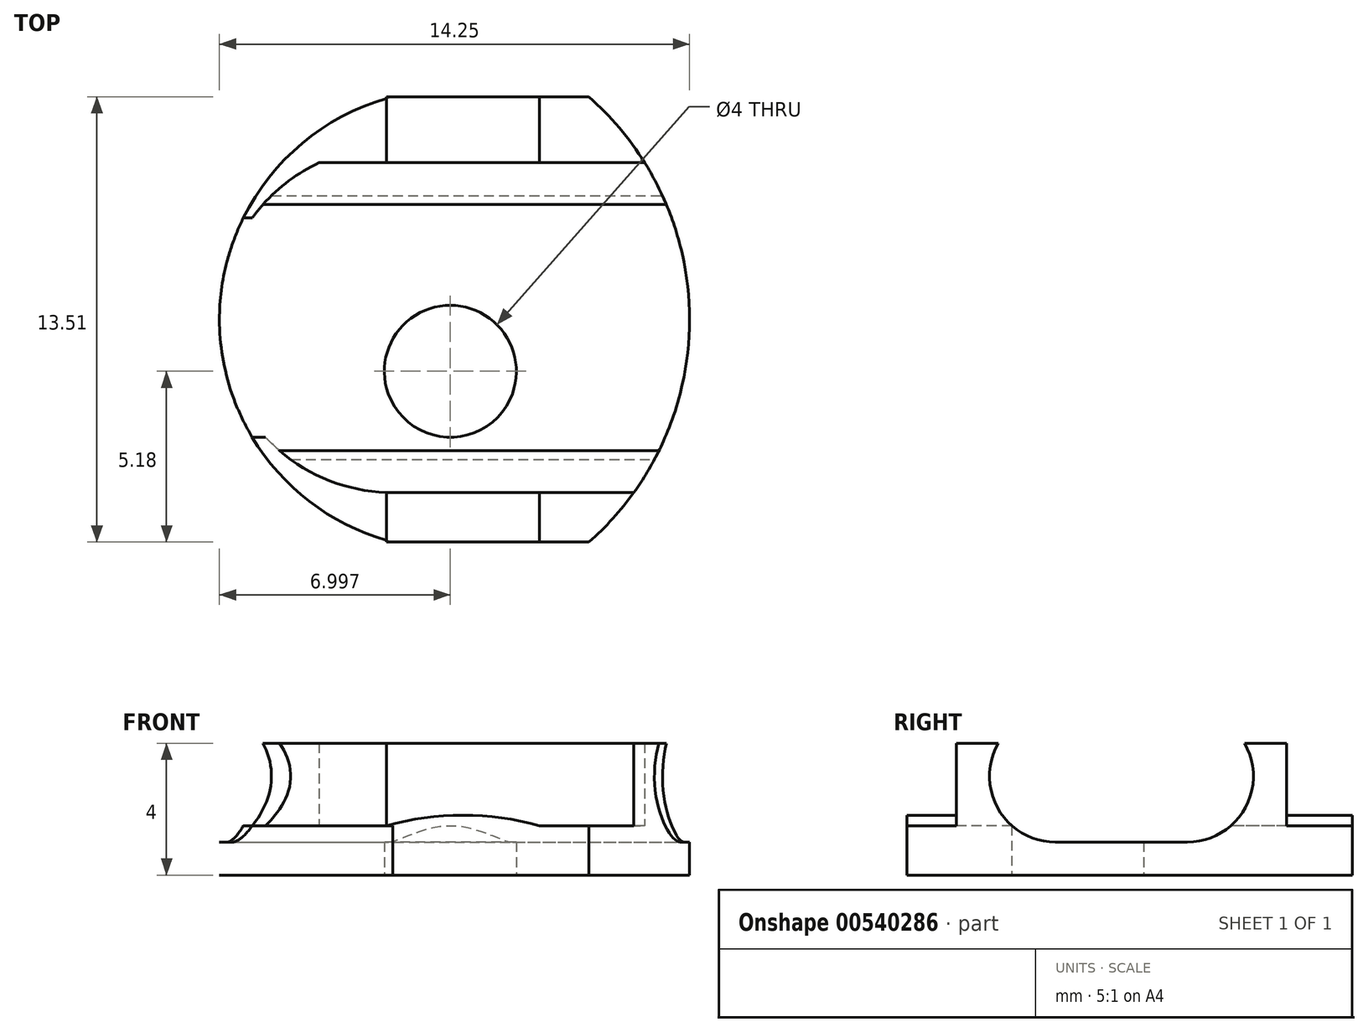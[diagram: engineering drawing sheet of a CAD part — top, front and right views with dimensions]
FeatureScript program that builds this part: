
annotation { "Feature Type Name" : "Feature", "Feature Type Description" : "" }
export const myFeature = defineFeature(function(context is Context, id is Id, definition is map)
    precondition{}
    {
        {
            var Q0;
            Q0=qCreatedBy(makeId("Top.planeOp"),FACE);
            var sketch = newSketch(context, id + "F0", { "sketchPlane" : qUnion([Q0])});
            skArc(sketch, "E0", {"start": v(-37.22, 31.39) * mm, "mid": v(-40.14, 25.58) * mm, "end": v(-35.18, 21.39) * mm});
            skLineSegment(sketch, "E1", {"start": v(-37.22, 31.39) * mm, "end": v(-29.22, 31.39) * mm});
            skLineSegment(sketch, "E2", {"start": v(-35.18, 21.39) * mm, "end": v(-27.87, 21.39) * mm});
            skLineSegment(sketch, "E3", {"start": v(-35, 33.38) * mm, "end": v(-29.04, 33.38) * mm});
            skLineSegment(sketch, "E4", {"start": v(-35, 19.88) * mm, "end": v(-29.04, 19.88) * mm});
            skArc(sketch, "E5", {"start": v(-29.04, 33.38) * mm, "mid": v(-26, 26.63) * mm, "end": v(-29.04, 19.88) * mm});
            skArc(sketch, "E6", {"start": v(-35, 33.38) * mm, "mid": v(-38.77, 30.9) * mm, "end": v(-40.24, 26.63) * mm});
            skArc(sketch, "E7", {"start": v(-40.24, 26.63) * mm, "mid": v(-38.77, 22.36) * mm, "end": v(-35, 19.88) * mm});
            skLineSegment(sketch, "E8.bottom", {"start": v(-29.22, 31.39) * mm, "end": v(-25.22, 31.39) * mm});
            skLineSegment(sketch, "E8.top", {"start": v(-29.22, 21.39) * mm, "end": v(-25.22, 21.39) * mm});
            skLineSegment(sketch, "E8.right", {"start": v(-25.22, 31.39) * mm, "end": v(-25.22, 21.39) * mm});
            skLineSegment(sketch, "E9", {"start": v(-33.24, 26.66) * mm, "end": v(-33.24, 25.06) * mm});
            skCircle(sketch, "E10", {"center": v(-33.24, 25.06) * mm, "radius": 2 * mm});
            skSolve(sketch);
        }
        {
            var Q0;
            {var subQ1=sQuery(id+"F0.wireOp",EDGE,"E1");Q0=makeQuery(id+"F0.imprint","IMPRINT",FACE,{"disambiguationData":[TD([[makeQuery(id+"F0.imprint","IMPRINT",EDGE,{"derivedFrom":subQ1}),-1.0]])]});}
            var Q1;
            {var subQ0=sQuery(id+"F0.wireOp",EDGE,"E8.bottom");Q1=makeQuery(id+"F0.imprint","IMPRINT",FACE,{"disambiguationData":[TD([[makeQuery(id+"F0.imprint","IMPRINT",EDGE,{"derivedFrom":subQ0}),-1.0]])]});}
            var Q2;
            Q2=makeQuery(id+"F0.imprint","IMPRINT",FACE,{"disambiguationData":[TD([[makeQuery(id+"F0.imprint","IMPRINT",EDGE,{"derivedFrom":sQuery(id+"F0.wireOp",EDGE,"E10")}),1.0]])]});
            extrude(context, id + "F1", {"entities" : qUnion([Q0, Q1, Q2]), "depth" : 4 * mm, "offsetDistance" : 25 * mm});
        }
        {
            var Q0;
            {var subQ1=sQuery(id+"F0.wireOp",EDGE,"E1");Q0=makeQuery(id+"F0.imprint","IMPRINT",FACE,{"disambiguationData":[TD([[makeQuery(id+"F0.imprint","IMPRINT",EDGE,{"derivedFrom":subQ1}),1.0]])]});}
            var Q1;
            {var subQ2=sQuery(id+"F0.wireOp",EDGE,"E2");Q1=makeQuery(id+"F0.imprint","IMPRINT",FACE,{"disambiguationData":[TD([[makeQuery(id+"F0.imprint","IMPRINT",EDGE,{"derivedFrom":subQ2}),-1.0]])]});}
            extrude(context, id + "F2", {"entities" : qUnion([Q0, Q1]), "operationType" : NewBodyOperationType.ADD, "depth" : 1.5 * mm, "offsetDistance" : 25 * mm});
        }
        {
            var Q0;
            Q0=makeQuery(id+"F1.opExtrude","SWEPT_FACE",FACE,{"disambiguationData":[OSD([sQuery(id+"F0.wireOp",EDGE,"E2")])]});
            var sketch = newSketch(context, id + "F3", { "sketchPlane" : qUnion([Q0])});
            skLineSegment(sketch, "E11", {"start": v(-29.04, 1.5) * mm, "end": v(-30.54, 1.5) * mm});
            skArc(sketch, "E12", {"start": v(-30.54, 1.5) * mm, "mid": v(-32.86, 1.82) * mm, "end": v(-35.18, 1.5) * mm});
            skSolve(sketch);
        }
        {
            var Q0;
            {var subQ0=sQuery(id+"F3.wireOp",EDGE,"E12");Q0=makeQuery(id+"F3.imprint","IMPRINT",FACE,{"disambiguationData":[TD([[makeQuery(id+"F3.imprint","IMPRINT",EDGE,{"derivedFrom":subQ0}),1.0]])]});}
            extrude(context, id + "F4", {"entities" : qUnion([Q0]), "operationType" : NewBodyOperationType.ADD, "oppositeDirection" : true, "depth" : 12 * mm, "offsetDistance" : 25 * mm});
        }
        {
            var Q0;
            {var subQ0=sQuery(id+"F3.wireOp",EDGE,"E12");Q0=makeQuery(id+"F3.imprint","IMPRINT",FACE,{"disambiguationData":[TD([[makeQuery(id+"F3.imprint","IMPRINT",EDGE,{"derivedFrom":subQ0}),1.0]])]});}
            extrude(context, id + "F5", {"entities" : qUnion([Q0]), "operationType" : NewBodyOperationType.ADD, "depth" : 1.5 * mm, "offsetDistance" : 25 * mm});
        }
        {
            var Q0;
            Q0=makeQuery(id+"F1.opExtrude","SWEPT_FACE",FACE,{"disambiguationData":[OSD([sQuery(id+"F0.wireOp",EDGE,"E8.right")])]});
            var sketch = newSketch(context, id + "F6", { "sketchPlane" : qUnion([Q0])});
            skLineSegment(sketch, "E13", {"start": v(21.39, 2) * mm, "end": v(21.39, 4) * mm});
            skPoint(sketch, "E14.centerSnap0", {"position": v(21.39, 3) * mm});
            skPoint(sketch, "E14.centerSnap1", {"position": v(26.39, 4) * mm});
            skPoint(sketch, "E15.startSnap0", {"position": v(31.39, 2) * mm});
            skLineSegment(sketch, "E16", {"start": v(28.39, 1) * mm, "end": v(24.39, 1) * mm});
            skLineSegment(sketch, "E17", {"start": v(24.39, 5) * mm, "end": v(28.39, 5) * mm});
            skArc(sketch, "E18", {"start": v(28.39, 5) * mm, "mid": v(30.39, 3) * mm, "end": v(28.39, 1) * mm});
            skArc(sketch, "E19", {"start": v(24.39, 5) * mm, "mid": v(22.39, 3) * mm, "end": v(24.39, 1) * mm});
            skCircle(sketch, "E20", {"center": v(28.39, 3) * mm, "radius": 2 * mm});
            skCircle(sketch, "E21", {"center": v(24.39, 3) * mm, "radius": 2 * mm});
            skSolve(sketch);
        }
        {
            var Q0;
            {var subQ0=sQuery(id+"F6.wireOp",EDGE,"E21");var subQ1=makeQuery(id+"F6.imprint","INTERSECT",VERTEX,{"derivedFrom":[sQuery(id+"F6.wireOp",EDGE,"E20"),subQ0]});Q0=makeQuery(id+"F6.imprint","IMPRINT",FACE,{"disambiguationData":[TD([[makeQuery(id+"F6.imprint","IMPRINT",EDGE,{"disambiguationData":[TD([[subQ1,-1.0]])],"derivedFrom":subQ0}),1.0]])]});}
            var Q1;
            {var subQ0=sQuery(id+"F6.wireOp",EDGE,"E16");Q1=makeQuery(id+"F6.imprint","IMPRINT",FACE,{"disambiguationData":[TD([[makeQuery(id+"F6.imprint","IMPRINT",EDGE,{"derivedFrom":subQ0}),-1.0]])]});}
            var Q2;
            {var subQ0=sQuery(id+"F6.wireOp",EDGE,"E20");var subQ1=makeQuery(id+"F6.imprint","INTERSECT",VERTEX,{"derivedFrom":[subQ0,sQuery(id+"F6.wireOp",EDGE,"E21")]});Q2=makeQuery(id+"F6.imprint","IMPRINT",FACE,{"disambiguationData":[TD([[makeQuery(id+"F6.imprint","IMPRINT",EDGE,{"disambiguationData":[TD([[subQ1,1.0]])],"derivedFrom":subQ0}),1.0]])]});}
            var Q3;
            {var subQ0=sQuery(id+"F6.wireOp",EDGE,"E21");var subQ1=sQuery(id+"F6.wireOp",EDGE,"E20");var subQ2=makeQuery(id+"F6.imprint","INTERSECT",VERTEX,{"derivedFrom":[subQ1,subQ0]});Q3=makeQuery(id+"F6.imprint","IMPRINT",FACE,{"disambiguationData":[TD([[makeQuery(id+"F6.imprint","IMPRINT",EDGE,{"disambiguationData":[TD([[subQ2,1.0]])],"derivedFrom":subQ1}),-1.0]])]});}
            extrude(context, id + "F7", {"entities" : qUnion([Q0, Q1, Q2, Q3]), "operationType" : NewBodyOperationType.REMOVE, "endBound" : BoundingType.THROUGH_ALL, "oppositeDirection" : true, "depth" : 25 * mm, "offsetDistance" : 25 * mm});
        }
        {
            var Q0;
            {var subQ0=sQuery(id+"F0.wireOp",EDGE,"E8.bottom");Q0=makeQuery(id+"F0.imprint","IMPRINT",FACE,{"disambiguationData":[TD([[makeQuery(id+"F0.imprint","IMPRINT",EDGE,{"derivedFrom":subQ0}),-1.0]])]});}
            extrude(context, id + "F8", {"entities" : qUnion([Q0]), "operationType" : NewBodyOperationType.REMOVE, "endBound" : BoundingType.THROUGH_ALL, "depth" : 25 * mm, "offsetDistance" : 25 * mm});
        }
        {
            var Q0;
            Q0=makeQuery(id+"F0.imprint","IMPRINT",FACE,{"disambiguationData":[TD([[makeQuery(id+"F0.imprint","IMPRINT",EDGE,{"derivedFrom":sQuery(id+"F0.wireOp",EDGE,"E10")}),1.0]])]});
            extrude(context, id + "F9", {"entities" : qUnion([Q0]), "operationType" : NewBodyOperationType.REMOVE, "depth" : 3 * mm, "offsetDistance" : 25 * mm});
        }
    });
